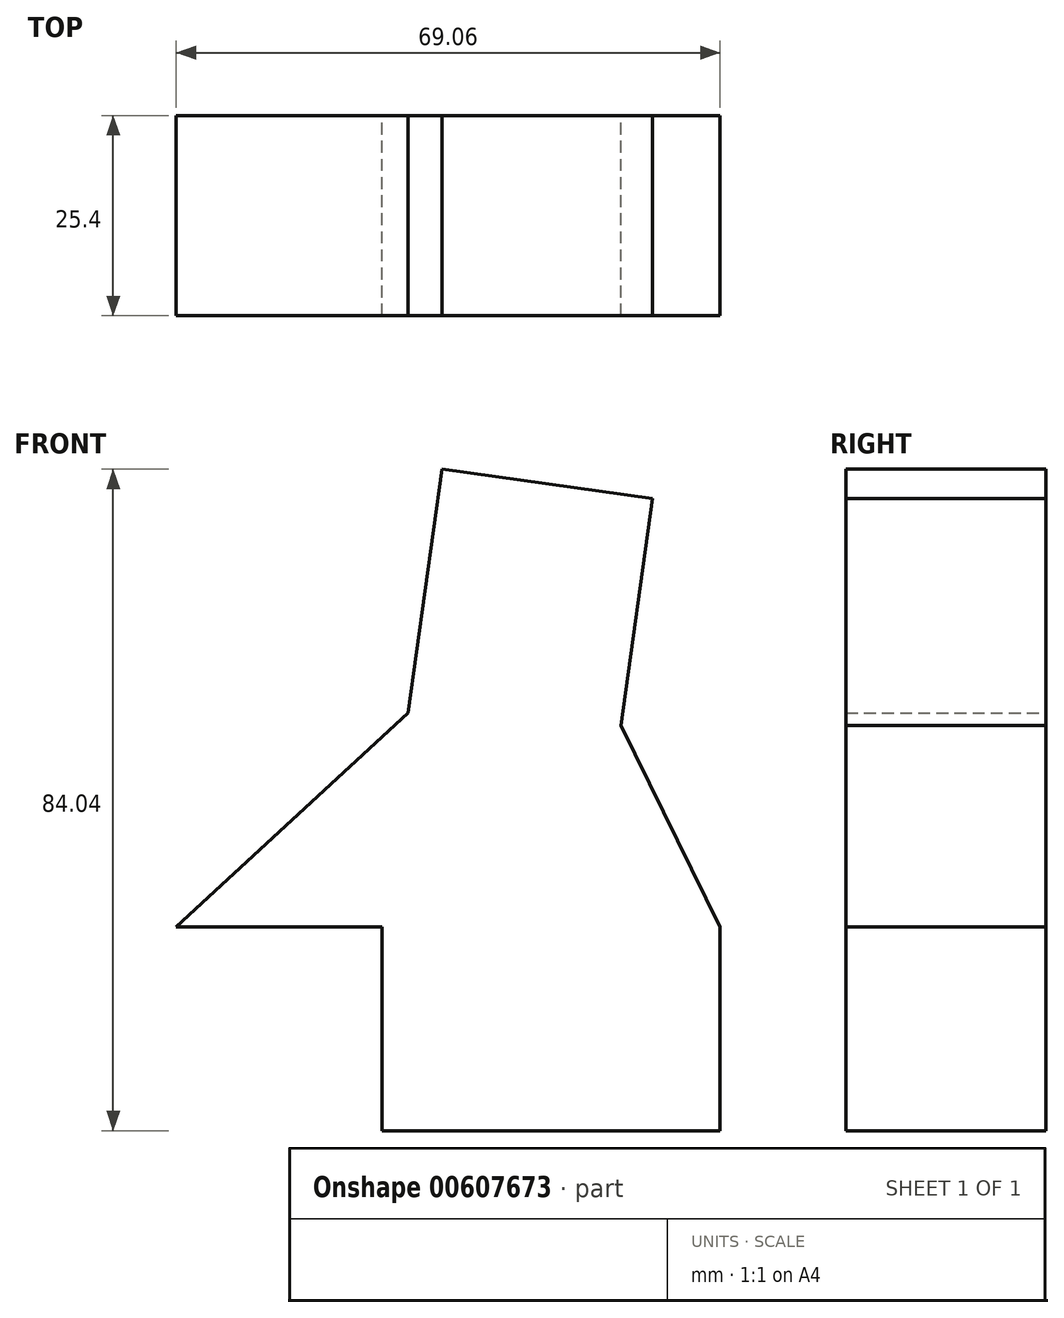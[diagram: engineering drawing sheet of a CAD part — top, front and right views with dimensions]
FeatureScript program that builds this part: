
annotation { "Feature Type Name" : "Feature", "Feature Type Description" : "" }
export const myFeature = defineFeature(function(context is Context, id is Id, definition is map)
    precondition{}
    {
        {
            var Q0;
            Q0=qCreatedBy(makeId("Front.planeOp"),FACE);
            var sketch = newSketch(context, id + "F0", { "sketchPlane" : qUnion([Q0])});
            skLineSegment(sketch, "E0", {"start": v(0, 0) * mm, "end": v(29.45, 27.17) * mm});
            skLineSegment(sketch, "E1", {"start": v(29.45, 27.17) * mm, "end": v(33.77, 58.14) * mm});
            skLineSegment(sketch, "E2", {"start": v(33.77, 58.14) * mm, "end": v(60.51, 54.41) * mm});
            skLineSegment(sketch, "E3", {"start": v(60.51, 54.41) * mm, "end": v(56.5, 25.55) * mm});
            skLineSegment(sketch, "E4", {"start": v(56.5, 25.55) * mm, "end": v(69.06, 0) * mm});
            skLineSegment(sketch, "E5", {"start": v(69.06, 0) * mm, "end": v(69.06, -25.9) * mm});
            skLineSegment(sketch, "E6", {"start": v(69.06, -25.9) * mm, "end": v(26.15, -25.9) * mm});
            skLineSegment(sketch, "E7", {"start": v(26.15, -25.9) * mm, "end": v(26.15, 0) * mm});
            skLineSegment(sketch, "E8", {"start": v(26.15, 0) * mm, "end": v(0, 0) * mm});
            skSolve(sketch);
        }
        {
            var Q0;
            Q0=makeQuery(id+"F0.imprint","IMPRINT",FACE,{"disambiguationData":[TD([[makeQuery(id+"F0.imprint","IMPRINT",EDGE,{"derivedFrom":sQuery(id+"F0.wireOp",EDGE,"E0")}),-1.0]])]});
            extrude(context, id + "F1", {"entities" : qUnion([Q0]), "depth" : 25.4 * mm, "offsetDistance" : 25.4 * mm});
        }
    });
